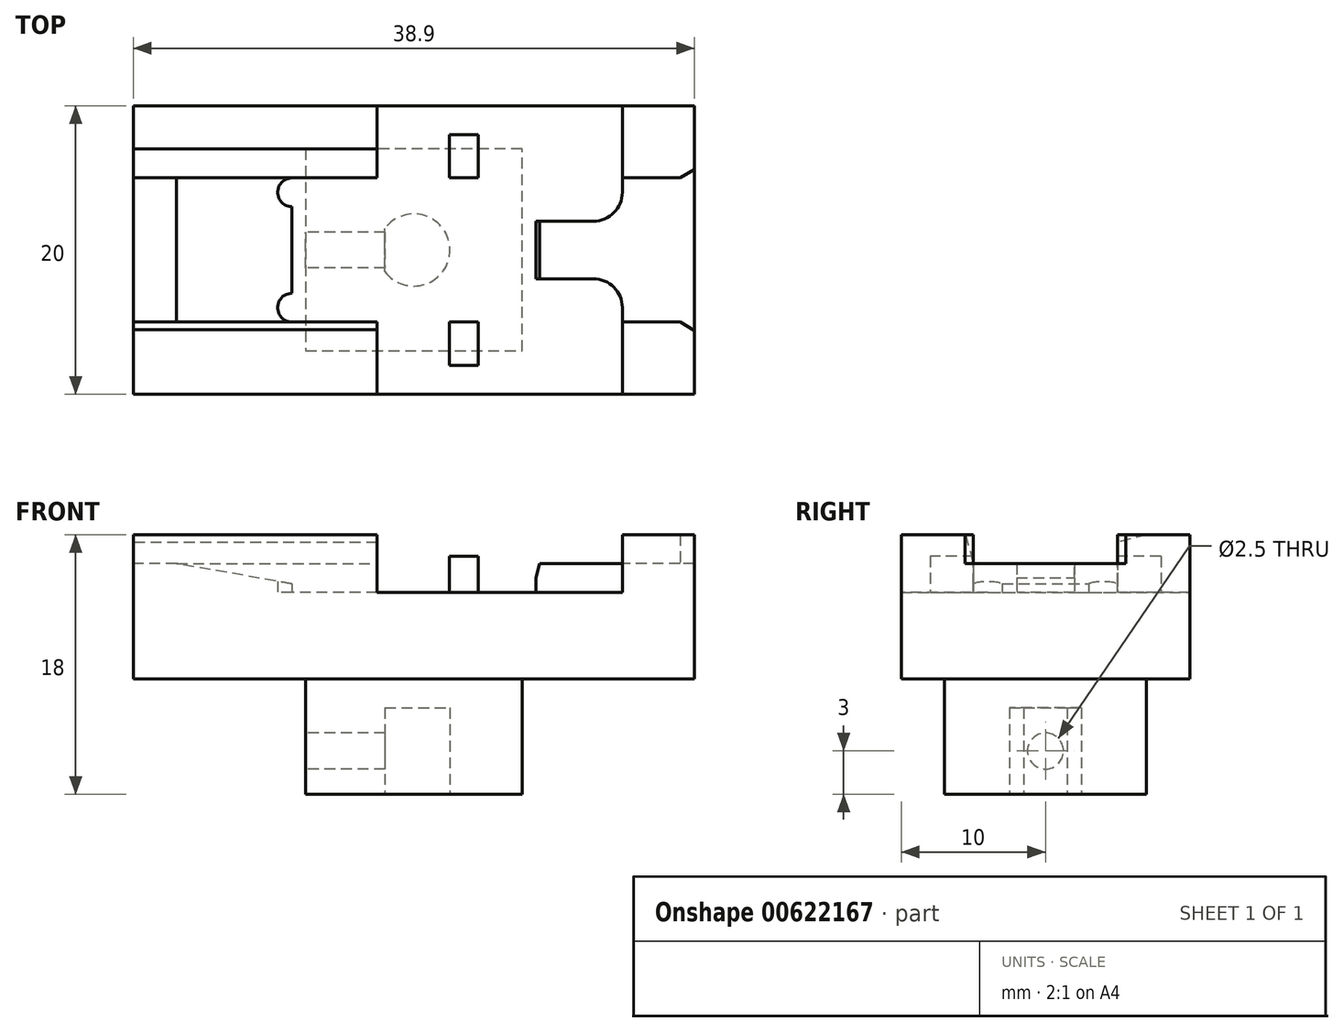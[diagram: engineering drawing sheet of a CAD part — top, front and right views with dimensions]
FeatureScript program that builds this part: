
annotation { "Feature Type Name" : "Feature", "Feature Type Description" : "" }
export const myFeature = defineFeature(function(context is Context, id is Id, definition is map)
    precondition{}
    {
        {
            var Q0;
            Q0=qCreatedBy(makeId("Top.planeOp"),FACE);
            var sketch = newSketch(context, id + "F0", { "sketchPlane" : qUnion([Q0])});
            skLineSegment(sketch, "E0", {"start": v(0, 10) * mm, "end": v(-19.45, 10) * mm});
            skLineSegment(sketch, "E1", {"start": v(-19.45, 10) * mm, "end": v(-19.45, -10) * mm});
            skLineSegment(sketch, "E2", {"start": v(-19.45, -10) * mm, "end": v(19.45, -10) * mm});
            skLineSegment(sketch, "E3", {"start": v(19.45, -10) * mm, "end": v(19.45, 10) * mm});
            skLineSegment(sketch, "E4", {"start": v(19.45, 10) * mm, "end": v(0, 10) * mm});
            skSolve(sketch);
        }
        {
            var Q0;
            Q0=makeQuery(id+"F0.imprint","IMPRINT",FACE,{"disambiguationData":[TD([[makeQuery(id+"F0.imprint","IMPRINT",EDGE,{"derivedFrom":sQuery(id+"F0.wireOp",EDGE,"E0")}),1.0]])]});
            extrude(context, id + "F1", {"entities" : qUnion([Q0]), "endBound" : BoundingType.SYMMETRIC, "depth" : 6 * mm, "offsetDistance" : 25 * mm});
        }
        {
            var Q0;
            Q0=qCreatedBy(makeId("Front.planeOp"),FACE);
            var sketch = newSketch(context, id + "F2", { "sketchPlane" : qUnion([Q0])});
            skLineSegment(sketch, "E5.0", {"start": v(-16.45, 5) * mm, "end": v(-19.45, 5) * mm});
            skLineSegment(sketch, "E6.0", {"start": v(-19.45, 3) * mm, "end": v(-8.45, 3) * mm});
            skLineSegment(sketch, "E7", {"start": v(-8.45, 3.59) * mm, "end": v(-16.45, 5) * mm});
            skLineSegment(sketch, "E8", {"start": v(-19.45, 5) * mm, "end": v(-19.45, 3) * mm});
            skLineSegment(sketch, "E9", {"start": v(-8.45, 3) * mm, "end": v(-8.45, 3.59) * mm});
            skSolve(sketch);
        }
        {
            var Q0;
            Q0 = qSketchRegion(id + "F2", true);
            extrude(context, id + "F3", {"entities" : qUnion([Q0]), "operationType" : NewBodyOperationType.ADD, "endBound" : BoundingType.SYMMETRIC, "depth" : 10 * mm, "offsetDistance" : 25 * mm});
        }
        {
            var Q0;
            Q0=makeQuery(id+"F1.opExtrude","CAP_FACE",FACE,{"disambiguationData":[OSD([sQuery(id+"F0.wireOp",EDGE,"E0"),sQuery(id+"F0.wireOp",EDGE,"E1"),sQuery(id+"F0.wireOp",EDGE,"E2"),sQuery(id+"F0.wireOp",EDGE,"E3"),sQuery(id+"F0.wireOp",EDGE,"E4")])],"isStart":false});
            var sketch = newSketch(context, id + "F4", { "sketchPlane" : qUnion([Q0])});
            skLineSegment(sketch, "E10", {"start": v(-8.45, 5) * mm, "end": v(-8.45, 4) * mm});
            skLineSegment(sketch, "E11", {"start": v(-8.45, -5) * mm, "end": v(-8.45, -4) * mm});
            skSolve(sketch);
        }
        {
            var Q0;
            Q0=sQuery(id+"F4.wireOp",VERTEX,"E10.end");
            var Q1;
            Q1=sQuery(id+"F4.wireOp",VERTEX,"E11.end");
            var Q2;
            Q2=makeQuery(id+"F1.opExtrude","SWEPT_BODY",BODY,{"disambiguationData":[OSD([sQuery(id+"F0.wireOp",EDGE,"E0"),sQuery(id+"F0.wireOp",EDGE,"E1"),sQuery(id+"F0.wireOp",EDGE,"E2"),sQuery(id+"F0.wireOp",EDGE,"E3"),sQuery(id+"F0.wireOp",EDGE,"E4")])]});
            hole(context, id + "F5", {"style" : HoleStyle.SIMPLE, "endStyle" : HoleEndStyle.THROUGH, "oppositeDirection" : true, "holeDiameter" : 2 * mm, "majorDiameter" : 5 * mm, "isTappedThrough" : true, "tappedDepth" : 2.9 * mm, "tapClearance" : 3, "startFromSketch" : true, "locations" : qUnion([Q0, Q1]), "scope" : qUnion([Q2])});
        }
        {
            var Q0;
            Q0=makeQuery(id+"F5.hole-1.boolean.opBoolean","MERGE",FACE,{"derivedFrom":[makeQuery(id+"F5.hole-0.boolean.opBoolean","MERGE",FACE,{"derivedFrom":[makeQuery(id+"F1.opExtrude","CAP_FACE",FACE,{"disambiguationData":[OSD([sQuery(id+"F0.wireOp",EDGE,"E0"),sQuery(id+"F0.wireOp",EDGE,"E1"),sQuery(id+"F0.wireOp",EDGE,"E2"),sQuery(id+"F0.wireOp",EDGE,"E3"),sQuery(id+"F0.wireOp",EDGE,"E4")])],"isStart":false}),makeQuery(id+"F5.hole-0.opRevolve","SWEPT_FACE",FACE,{"disambiguationData":[OSD([sQuery(id+"F5.hole-0.sketch.wireOp",EDGE,"core_line_3")])]})]}),makeQuery(id+"F5.hole-1.opRevolve","SWEPT_FACE",FACE,{"disambiguationData":[OSD([sQuery(id+"F5.hole-1.sketch.wireOp",EDGE,"core_line_3")])]})]});
            var sketch = newSketch(context, id + "F6", { "sketchPlane" : qUnion([Q0])});
            skLineSegment(sketch, "E12", {"start": v(-2.55, -10) * mm, "end": v(-2.55, -5) * mm});
            skLineSegment(sketch, "E13", {"start": v(-2.55, -5) * mm, "end": v(-19.45, -5) * mm});
            skLineSegment(sketch, "E14", {"start": v(-19.45, -5) * mm, "end": v(-19.45, -10) * mm});
            skLineSegment(sketch, "E15", {"start": v(-19.45, -10) * mm, "end": v(-2.55, -10) * mm});
            skLineSegment(sketch, "E16.MirrorCS", {"start": v(-19.45, 5) * mm, "end": v(-19.45, 10) * mm});
            skLineSegment(sketch, "E17.MirrorCS", {"start": v(-2.55, 5) * mm, "end": v(-19.45, 5) * mm});
            skLineSegment(sketch, "E18.MirrorCS", {"start": v(-2.55, 10) * mm, "end": v(-2.55, 5) * mm});
            skLineSegment(sketch, "E19.MirrorCS", {"start": v(-19.45, 10) * mm, "end": v(-2.55, 10) * mm});
            skLineSegment(sketch, "E20", {"start": v(19.45, -10) * mm, "end": v(19.45, -5) * mm});
            skLineSegment(sketch, "E21", {"start": v(19.45, -5) * mm, "end": v(14.45, -5) * mm});
            skLineSegment(sketch, "E22", {"start": v(14.45, -5) * mm, "end": v(14.45, -10) * mm});
            skLineSegment(sketch, "E23", {"start": v(14.45, -10) * mm, "end": v(19.45, -10) * mm});
            skLineSegment(sketch, "E24.MirrorCS", {"start": v(14.45, 5) * mm, "end": v(14.45, 10) * mm});
            skLineSegment(sketch, "E25.MirrorCS", {"start": v(19.45, 5) * mm, "end": v(14.45, 5) * mm});
            skLineSegment(sketch, "E26.MirrorCS", {"start": v(19.45, 10) * mm, "end": v(19.45, 5) * mm});
            skLineSegment(sketch, "E27.MirrorCS", {"start": v(14.45, 10) * mm, "end": v(19.45, 10) * mm});
            skSolve(sketch);
        }
        {
            var Q0;
            {var subQ3=sQuery(id+"F6.wireOp",EDGE,"E12");Q0=makeQuery(id+"F6.imprint","IMPRINT",FACE,{"disambiguationData":[TD([[makeQuery(id+"F6.imprint","IMPRINT",EDGE,{"derivedFrom":subQ3}),1.0]])]});}
            var Q1;
            {var subQ2=sQuery(id+"F6.wireOp",EDGE,"E16.MirrorCS");Q1=makeQuery(id+"F6.imprint","IMPRINT",FACE,{"disambiguationData":[TD([[makeQuery(id+"F6.imprint","IMPRINT",EDGE,{"derivedFrom":subQ2}),1.0]])]});}
            var Q2;
            Q2=makeQuery(id+"F6.imprint","IMPRINT",FACE,{"disambiguationData":[TD([[makeQuery(id+"F6.imprint","IMPRINT",EDGE,{"derivedFrom":sQuery(id+"F6.wireOp",EDGE,"E24.MirrorCS")}),-1.0]])]});
            var Q3;
            Q3=makeQuery(id+"F6.imprint","IMPRINT",FACE,{"disambiguationData":[TD([[makeQuery(id+"F6.imprint","IMPRINT",EDGE,{"derivedFrom":sQuery(id+"F6.wireOp",EDGE,"E20")}),1.0]])]});
            extrude(context, id + "F7", {"entities" : qUnion([Q0, Q1, Q2, Q3]), "operationType" : NewBodyOperationType.ADD, "depth" : 4 * mm, "offsetDistance" : 25 * mm});
        }
        {
            var Q0;
            Q0=makeQuery(id+"F5.hole-1.boolean.opBoolean","MERGE",FACE,{"derivedFrom":[makeQuery(id+"F5.hole-0.boolean.opBoolean","MERGE",FACE,{"derivedFrom":[makeQuery(id+"F1.opExtrude","CAP_FACE",FACE,{"disambiguationData":[OSD([sQuery(id+"F0.wireOp",EDGE,"E0"),sQuery(id+"F0.wireOp",EDGE,"E1"),sQuery(id+"F0.wireOp",EDGE,"E2"),sQuery(id+"F0.wireOp",EDGE,"E3"),sQuery(id+"F0.wireOp",EDGE,"E4")])],"isStart":false}),makeQuery(id+"F5.hole-0.opRevolve","SWEPT_FACE",FACE,{"disambiguationData":[OSD([sQuery(id+"F5.hole-0.sketch.wireOp",EDGE,"core_line_3")])]})]}),makeQuery(id+"F5.hole-1.opRevolve","SWEPT_FACE",FACE,{"disambiguationData":[OSD([sQuery(id+"F5.hole-1.sketch.wireOp",EDGE,"core_line_3")])]})]});
            var sketch = newSketch(context, id + "F8", { "sketchPlane" : qUnion([Q0])});
            skLineSegment(sketch, "E28", {"start": v(4.45, -8) * mm, "end": v(2.45, -8) * mm});
            skLineSegment(sketch, "E29", {"start": v(2.45, -8) * mm, "end": v(2.45, -5) * mm});
            skLineSegment(sketch, "E30", {"start": v(2.45, -5) * mm, "end": v(4.45, -5) * mm});
            skLineSegment(sketch, "E31", {"start": v(4.45, -5) * mm, "end": v(4.45, -8) * mm});
            skLineSegment(sketch, "E32.MirrorCS", {"start": v(2.45, 8) * mm, "end": v(2.45, 5) * mm});
            skLineSegment(sketch, "E33.MirrorCS", {"start": v(4.45, 8) * mm, "end": v(2.45, 8) * mm});
            skLineSegment(sketch, "E34.MirrorCS", {"start": v(4.45, 5) * mm, "end": v(4.45, 8) * mm});
            skLineSegment(sketch, "E35.MirrorCS", {"start": v(2.45, 5) * mm, "end": v(4.45, 5) * mm});
            skSolve(sketch);
        }
        {
            var Q0;
            Q0=makeQuery(id+"F8.imprint","IMPRINT",FACE,{"disambiguationData":[TD([[makeQuery(id+"F8.imprint","IMPRINT",EDGE,{"derivedFrom":sQuery(id+"F8.wireOp",EDGE,"E32.MirrorCS")}),1.0]])]});
            var Q1;
            Q1=makeQuery(id+"F8.imprint","IMPRINT",FACE,{"disambiguationData":[TD([[makeQuery(id+"F8.imprint","IMPRINT",EDGE,{"derivedFrom":sQuery(id+"F8.wireOp",EDGE,"E28")}),-1.0]])]});
            extrude(context, id + "F9", {"entities" : qUnion([Q0, Q1]), "operationType" : NewBodyOperationType.ADD, "depth" : 2.5 * mm, "offsetDistance" : 25 * mm});
        }
        {
            var Q0;
            Q0=makeQuery(id+"F5.hole-1.boolean.opBoolean","MERGE",FACE,{"derivedFrom":[makeQuery(id+"F5.hole-0.boolean.opBoolean","MERGE",FACE,{"derivedFrom":[makeQuery(id+"F1.opExtrude","CAP_FACE",FACE,{"disambiguationData":[OSD([sQuery(id+"F0.wireOp",EDGE,"E0"),sQuery(id+"F0.wireOp",EDGE,"E1"),sQuery(id+"F0.wireOp",EDGE,"E2"),sQuery(id+"F0.wireOp",EDGE,"E3"),sQuery(id+"F0.wireOp",EDGE,"E4")])],"isStart":false}),makeQuery(id+"F5.hole-0.opRevolve","SWEPT_FACE",FACE,{"disambiguationData":[OSD([sQuery(id+"F5.hole-0.sketch.wireOp",EDGE,"core_line_3")])]})]}),makeQuery(id+"F5.hole-1.opRevolve","SWEPT_FACE",FACE,{"disambiguationData":[OSD([sQuery(id+"F5.hole-1.sketch.wireOp",EDGE,"core_line_3")])]})]});
            var sketch = newSketch(context, id + "F10", { "sketchPlane" : qUnion([Q0])});
            skLineSegment(sketch, "E36", {"start": v(19.45, 5) * mm, "end": v(14.45, 5) * mm});
            skLineSegment(sketch, "E37", {"start": v(14.45, 5) * mm, "end": v(14.45, 2) * mm});
            skLineSegment(sketch, "E38", {"start": v(14.45, 2) * mm, "end": v(8.45, 2) * mm});
            skLineSegment(sketch, "E39", {"start": v(8.45, 2) * mm, "end": v(8.45, -2) * mm});
            skLineSegment(sketch, "E40", {"start": v(8.45, -2) * mm, "end": v(14.45, -2) * mm});
            skLineSegment(sketch, "E41", {"start": v(14.45, -2) * mm, "end": v(14.45, -5) * mm});
            skLineSegment(sketch, "E42", {"start": v(14.45, -5) * mm, "end": v(19.45, -5) * mm});
            skLineSegment(sketch, "E43", {"start": v(19.45, -5) * mm, "end": v(19.45, 5) * mm});
            skSolve(sketch);
        }
        {
            var Q0;
            Q0=makeQuery(id+"F10.imprint","IMPRINT",FACE,{"disambiguationData":[TD([[makeQuery(id+"F10.imprint","IMPRINT",EDGE,{"derivedFrom":sQuery(id+"F10.wireOp",EDGE,"E36")}),1.0]])]});
            extrude(context, id + "F11", {"entities" : qUnion([Q0]), "operationType" : NewBodyOperationType.ADD, "depth" : 2 * mm, "offsetDistance" : 25 * mm});
        }
        {
            var Q0;
            Q0=makeQuery(id+"F11.opExtrude","SWEPT_EDGE",EDGE,{"disambiguationData":[OSD([sQuery(id+"F10.wireOp",EDGE,"E40"),sQuery(id+"F10.wireOp",EDGE,"E41")])]});
            var Q1;
            Q1=makeQuery(id+"F11.opExtrude","SWEPT_EDGE",EDGE,{"disambiguationData":[OSD([sQuery(id+"F10.wireOp",EDGE,"E37"),sQuery(id+"F10.wireOp",EDGE,"E38")])]});
            fillet(context, id + "F12", {"entities" : qUnion([Q0, Q1]), "radius" : 2 * mm, "tangentPropagation" : true, "allowEdgeOverflow" : false});
        }
        {
            var Q0;
            Q0=makeQuery(id+"F11.opExtrude","CAP_EDGE",EDGE,{"disambiguationData":[OSD([sQuery(id+"F10.wireOp",EDGE,"E39")])],"isStart":false});
            chamfer(context, id + "F13", {"entities" : qUnion([Q0]), "chamferType" : ChamferType.OFFSET_ANGLE, "width" : 1 * mm, "oppositeDirection" : true, "angle" : 15 * degree, "tangentPropagation" : true});
        }
        {
            var Q0;
            Q0=makeQuery(id+"F7.opExtrude","CAP_EDGE",EDGE,{"disambiguationData":[OSD([sQuery(id+"F6.wireOp",EDGE,"E17.MirrorCS")])],"isStart":false});
            var Q1;
            Q1=makeQuery(id+"F7.opExtrude","CAP_EDGE",EDGE,{"disambiguationData":[OSD([sQuery(id+"F6.wireOp",EDGE,"E13")])],"isStart":false});
            chamfer(context, id + "F14", {"entities" : qUnion([Q0, Q1]), "chamferType" : ChamferType.OFFSET_ANGLE, "width" : 2 * mm, "oppositeDirection" : true, "angle" : 15 * degree, "tangentPropagation" : true});
        }
        {
            var Q0;
            Q0=makeQuery(id+"F7.opExtrude","SWEPT_EDGE",EDGE,{"disambiguationData":[OSD([sQuery(id+"F0.wireOp",EDGE,"E3"),sQuery(id+"F6.wireOp",EDGE,"E25.MirrorCS"),sQuery(id+"F6.wireOp",EDGE,"E26.MirrorCS")])]});
            var Q1;
            Q1=makeQuery(id+"F7.opExtrude","SWEPT_EDGE",EDGE,{"disambiguationData":[OSD([sQuery(id+"F0.wireOp",EDGE,"E3"),sQuery(id+"F6.wireOp",EDGE,"E20"),sQuery(id+"F6.wireOp",EDGE,"E21")])]});
            chamfer(context, id + "F15", {"entities" : qUnion([Q0, Q1]), "chamferType" : ChamferType.OFFSET_ANGLE, "width" : 1 * mm, "oppositeDirection" : true, "angle" : 30 * degree, "tangentPropagation" : true});
        }
        {
            var Q0;
            Q0=makeQuery(id+"F1.opExtrude","CAP_FACE",FACE,{"disambiguationData":[OSD([sQuery(id+"F0.wireOp",EDGE,"E0"),sQuery(id+"F0.wireOp",EDGE,"E1"),sQuery(id+"F0.wireOp",EDGE,"E2"),sQuery(id+"F0.wireOp",EDGE,"E3"),sQuery(id+"F0.wireOp",EDGE,"E4")])],"isStart":true});
            var sketch = newSketch(context, id + "F16", { "sketchPlane" : qUnion([Q0])});
            skLineSegment(sketch, "E44", {"start": v(-7.5, -7) * mm, "end": v(-7.5, 7) * mm});
            skLineSegment(sketch, "E45", {"start": v(-7.5, 7) * mm, "end": v(7.5, 7) * mm});
            skLineSegment(sketch, "E46", {"start": v(7.5, 7) * mm, "end": v(7.5, -7) * mm});
            skLineSegment(sketch, "E47", {"start": v(7.5, -7) * mm, "end": v(-7.5, -7) * mm});
            skSolve(sketch);
        }
        {
            var Q0;
            Q0=makeQuery(id+"F16.imprint","IMPRINT",FACE,{"disambiguationData":[TD([[makeQuery(id+"F16.imprint","IMPRINT",EDGE,{"derivedFrom":sQuery(id+"F16.wireOp",EDGE,"E44")}),-1.0]])]});
            extrude(context, id + "F17", {"entities" : qUnion([Q0]), "operationType" : NewBodyOperationType.ADD, "depth" : 8 * mm, "offsetDistance" : 25 * mm});
        }
        {
            var Q0;
            Q0=makeQuery(id+"F17.opExtrude","CAP_FACE",FACE,{"disambiguationData":[OSD([sQuery(id+"F16.wireOp",EDGE,"E44"),sQuery(id+"F16.wireOp",EDGE,"E45"),sQuery(id+"F16.wireOp",EDGE,"E46"),sQuery(id+"F16.wireOp",EDGE,"E47")])],"isStart":false});
            var sketch = newSketch(context, id + "F18", { "sketchPlane" : qUnion([Q0])});
            skArc(sketch, "E48", {"start": v(-2, -1.5) * mm, "mid": v(2.5, 0) * mm, "end": v(-2, 1.5) * mm});
            skLineSegment(sketch, "E49", {"start": v(-2, 0) * mm, "end": v(-2, 1.5) * mm});
            skLineSegment(sketch, "E50", {"start": v(-2, 0) * mm, "end": v(-2, -1.5) * mm});
            skSolve(sketch);
        }
        {
            var Q0;
            Q0=makeQuery(id+"F18.imprint","IMPRINT",FACE,{"disambiguationData":[TD([[makeQuery(id+"F18.imprint","IMPRINT",EDGE,{"derivedFrom":sQuery(id+"F18.wireOp",EDGE,"E48")}),1.0]])]});
            extrude(context, id + "F19", {"entities" : qUnion([Q0]), "operationType" : NewBodyOperationType.REMOVE, "oppositeDirection" : true, "depth" : 6 * mm, "offsetDistance" : 25 * mm});
        }
        {
            var Q0;
            Q0=makeQuery(id+"F17.opExtrude","SWEPT_FACE",FACE,{"disambiguationData":[OSD([sQuery(id+"F16.wireOp",EDGE,"E44")])]});
            var sketch = newSketch(context, id + "F20", { "sketchPlane" : qUnion([Q0])});
            skLineSegment(sketch, "E51", {"start": v(0, -11) * mm, "end": v(0, -8) * mm});
            skSolve(sketch);
        }
        {
            var Q0;
            Q0=sQuery(id+"F20.wireOp",VERTEX,"E51.end");
            var Q1;
            Q1=makeQuery(id+"F1.opExtrude","SWEPT_BODY",BODY,{"disambiguationData":[OSD([sQuery(id+"F0.wireOp",EDGE,"E0"),sQuery(id+"F0.wireOp",EDGE,"E1"),sQuery(id+"F0.wireOp",EDGE,"E2"),sQuery(id+"F0.wireOp",EDGE,"E3"),sQuery(id+"F0.wireOp",EDGE,"E4")])]});
            hole(context, id + "F21", {"style" : HoleStyle.SIMPLE, "endStyle" : HoleEndStyle.BLIND, "standardTappedOrClearance" : lookupTablePath({ "standard" : "ISO", "engagement" : "75%", "pitch" : "0.5 mm", "size" : "M3", "type" : "Tapped" }), "standardBlindInLast" : lookupTablePath({ "standard" : "ISO", "engagement" : "75%", "pitch" : "0.5 mm", "size" : "M3", "type" : "Tapped" }), "holeDiameter" : 2.5 * mm, "majorDiameter" : 3 * mm, "showTappedDepth" : true, "holeDepth" : 7.5 * mm, "isTappedThrough" : true, "tappedDepth" : 6 * mm, "tapClearance" : 3, "startFromSketch" : true, "locations" : qUnion([Q0]), "scope" : qUnion([Q1])});
        }
    });
